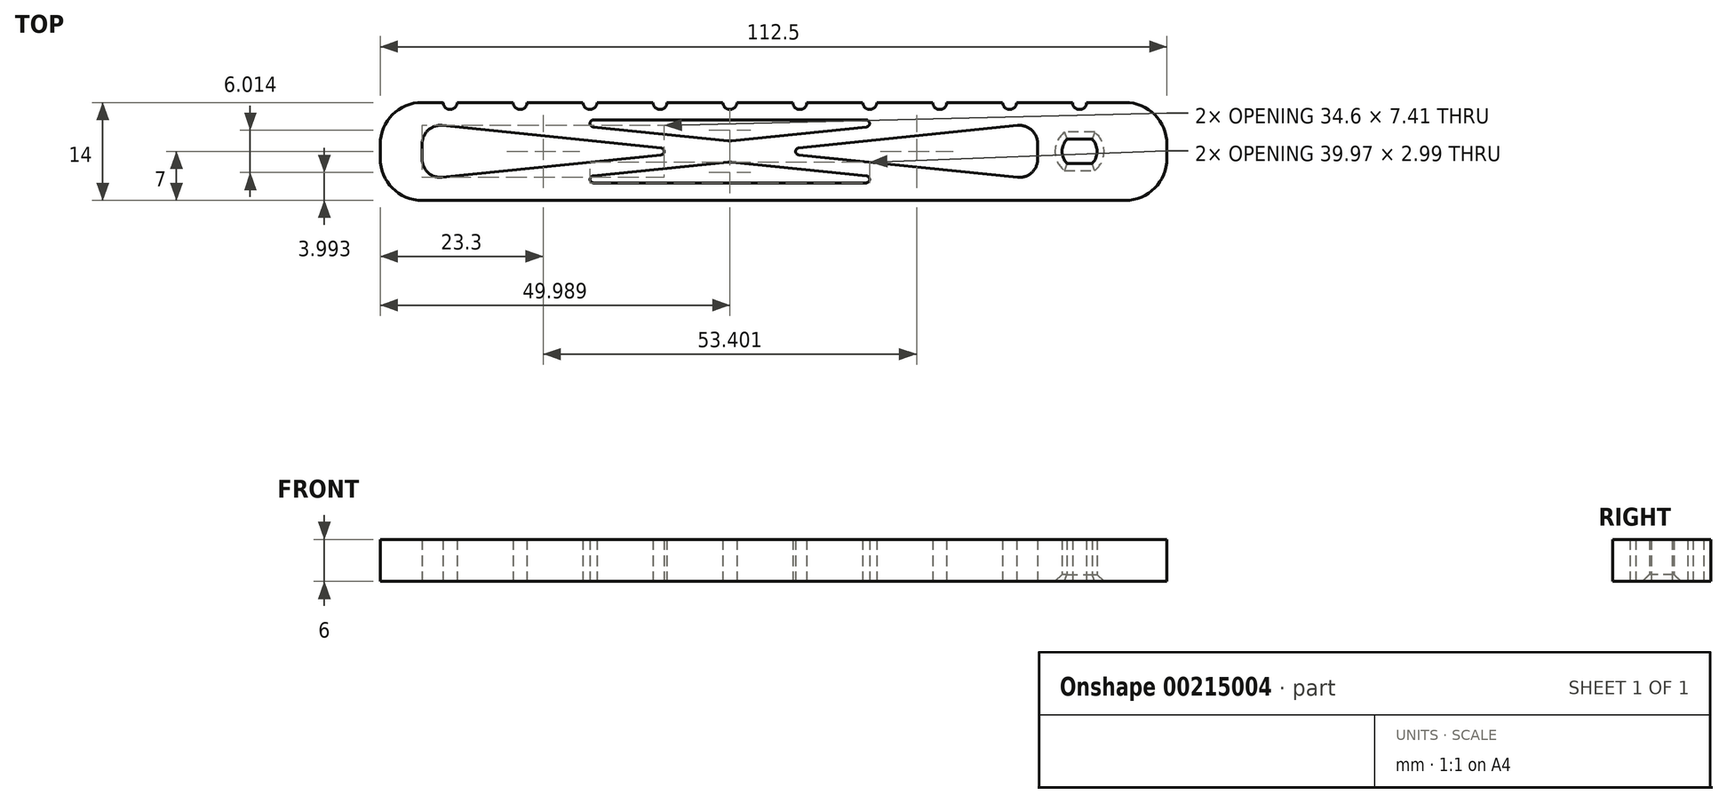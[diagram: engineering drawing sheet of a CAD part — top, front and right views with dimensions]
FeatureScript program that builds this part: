
annotation { "Feature Type Name" : "Feature", "Feature Type Description" : "" }
export const myFeature = defineFeature(function(context is Context, id is Id, definition is map)
    precondition{}
    {
        {
            var Q0;
            Q0=qCreatedBy(makeId("Top.planeOp"),FACE);
            var sketch = newSketch(context, id + "F0", { "sketchPlane" : qUnion([Q0])});
            skLineSegment(sketch, "E0.bottom", {"start": v(-94, 7) * mm, "end": v(-91, 7) * mm});
            skLineSegment(sketch, "E0.top", {"start": v(-94, -7) * mm, "end": v(6.5, -7) * mm});
            skLineSegment(sketch, "E0.left", {"start": v(-100, 1) * mm, "end": v(-100, -1) * mm});
            skLineSegment(sketch, "E0.right", {"start": v(12.5, 1) * mm, "end": v(12.5, -1) * mm});
            skArc(sketch, "E1", {"start": v(-1.79, 1.75) * mm, "mid": v(-2.5, 0) * mm, "end": v(-1.79, -1.75) * mm});
            skLineSegment(sketch, "E2.bottom", {"start": v(-1.79, 1.75) * mm, "end": v(1.79, 1.75) * mm});
            skLineSegment(sketch, "E2.top", {"start": v(-1.79, -1.75) * mm, "end": v(1.79, -1.75) * mm});
            skArc(sketch, "E3.trimOffspring", {"start": v(1.79, -1.75) * mm, "mid": v(2.5, 0) * mm, "end": v(1.79, 1.75) * mm});
            skPoint(sketch, "E4.visualSharp", {"position": v(12.5, 7) * mm});
            skArc(sketch, "E4.filletArc", {"start": v(12.5, 1) * mm, "mid": v(10.74, 5.24) * mm, "end": v(6.5, 7) * mm});
            skPoint(sketch, "E5.visualSharp", {"position": v(12.5, -7) * mm});
            skArc(sketch, "E5.filletArc", {"start": v(6.5, -7) * mm, "mid": v(10.74, -5.24) * mm, "end": v(12.5, -1) * mm});
            skPoint(sketch, "E6.visualSharp", {"position": v(-100, 7) * mm});
            skArc(sketch, "E6.filletArc", {"start": v(-94, 7) * mm, "mid": v(-98.24, 5.24) * mm, "end": v(-100, 1) * mm});
            skPoint(sketch, "E7.visualSharp", {"position": v(-100, -7) * mm});
            skArc(sketch, "E7.filletArc", {"start": v(-100, -1) * mm, "mid": v(-98.24, -5.24) * mm, "end": v(-94, -7) * mm});
            skArc(sketch, "E8", {"start": v(-1, 7) * mm, "mid": v(0, 6) * mm, "end": v(1, 7) * mm});
            skLineSegment(sketch, "E9.trimOffspring", {"start": v(1, 7) * mm, "end": v(6.5, 7) * mm});
            skArc(sketch, "E10.1.0.0", {"start": v(-11, 7) * mm, "mid": v(-10, 6) * mm, "end": v(-9, 7) * mm});
            skArc(sketch, "E10.2.0.0", {"start": v(-21, 7) * mm, "mid": v(-20, 6) * mm, "end": v(-19, 7) * mm});
            skArc(sketch, "E10.3.0.0", {"start": v(-31, 7) * mm, "mid": v(-30, 6) * mm, "end": v(-29, 7) * mm});
            skArc(sketch, "E10.4.0.0", {"start": v(-41, 7) * mm, "mid": v(-40, 6) * mm, "end": v(-39, 7) * mm});
            skArc(sketch, "E10.5.0.0", {"start": v(-51, 7) * mm, "mid": v(-50, 6) * mm, "end": v(-49, 7) * mm});
            skArc(sketch, "E10.6.0.0", {"start": v(-61, 7) * mm, "mid": v(-60, 6) * mm, "end": v(-59, 7) * mm});
            skArc(sketch, "E10.7.0.0", {"start": v(-71, 7) * mm, "mid": v(-70, 6) * mm, "end": v(-69, 7) * mm});
            skArc(sketch, "E10.8.0.0", {"start": v(-81, 7) * mm, "mid": v(-80, 6) * mm, "end": v(-79, 7) * mm});
            skArc(sketch, "E10.9.0.0", {"start": v(-91, 7) * mm, "mid": v(-90, 6) * mm, "end": v(-89, 7) * mm});
            skLineSegment(sketch, "E11.trimOffspring", {"start": v(-89, 7) * mm, "end": v(-81, 7) * mm});
            skLineSegment(sketch, "E12.trimOffspring", {"start": v(-79, 7) * mm, "end": v(-71, 7) * mm});
            skLineSegment(sketch, "E13.trimOffspring", {"start": v(-69, 7) * mm, "end": v(-61, 7) * mm});
            skLineSegment(sketch, "E14.trimOffspring", {"start": v(-59, 7) * mm, "end": v(-51, 7) * mm});
            skLineSegment(sketch, "E15.trimOffspring", {"start": v(-49, 7) * mm, "end": v(-41, 7) * mm});
            skLineSegment(sketch, "E16.trimOffspring", {"start": v(-39, 7) * mm, "end": v(-31, 7) * mm});
            skLineSegment(sketch, "E17.trimOffspring", {"start": v(-29, 7) * mm, "end": v(-21, 7) * mm});
            skLineSegment(sketch, "E18.trimOffspring", {"start": v(-19, 7) * mm, "end": v(-11, 7) * mm});
            skLineSegment(sketch, "E19.trimOffspring", {"start": v(-9, 7) * mm, "end": v(-1, 7) * mm});
            skLineSegment(sketch, "E20", {"start": v(-94, 1.12) * mm, "end": v(-94, -1.12) * mm});
            skLineSegment(sketch, "E21", {"start": v(-91.13, -3.7) * mm, "end": v(-59.85, -0.5) * mm});
            skLineSegment(sketch, "E22", {"start": v(-59.85, 0.5) * mm, "end": v(-91.13, 3.7) * mm});
            skLineSegment(sketch, "E23", {"start": v(-40.15, 0.5) * mm, "end": v(-8.87, 3.7) * mm});
            skLineSegment(sketch, "E24", {"start": v(-6, 1.12) * mm, "end": v(-6, -1.12) * mm});
            skLineSegment(sketch, "E25", {"start": v(-8.87, -3.7) * mm, "end": v(-40.15, -0.5) * mm});
            skLineSegment(sketch, "E26", {"start": v(-69.5, 4.5) * mm, "end": v(-30.53, 4.5) * mm});
            skLineSegment(sketch, "E27", {"start": v(-30.47, 3.5) * mm, "end": v(-49.76, 1.53) * mm});
            skLineSegment(sketch, "E28", {"start": v(-50.29, 1.53) * mm, "end": v(-69.55, 3.5) * mm});
            skLineSegment(sketch, "E29", {"start": v(-69.55, -3.5) * mm, "end": v(-50.29, -1.53) * mm});
            skLineSegment(sketch, "E30", {"start": v(-49.76, -1.53) * mm, "end": v(-30.47, -3.5) * mm});
            skLineSegment(sketch, "E31", {"start": v(-30.53, -4.5) * mm, "end": v(-69.5, -4.5) * mm});
            skPoint(sketch, "E32.visualSharp", {"position": v(-94, 4) * mm});
            skArc(sketch, "E32.filletArc", {"start": v(-91.13, 3.7) * mm, "mid": v(-93.14, 3.05) * mm, "end": v(-94, 1.12) * mm});
            skPoint(sketch, "E33.visualSharp", {"position": v(-94, -4) * mm});
            skArc(sketch, "E33.filletArc", {"start": v(-94, -1.12) * mm, "mid": v(-93.14, -3.05) * mm, "end": v(-91.13, -3.7) * mm});
            skPoint(sketch, "E34.visualSharp", {"position": v(-50.02, -1.5) * mm});
            skArc(sketch, "E34.filletArc", {"start": v(-49.76, -1.53) * mm, "mid": v(-50.02, -1.51) * mm, "end": v(-50.29, -1.53) * mm});
            skPoint(sketch, "E35.visualSharp", {"position": v(-50.02, 1.5) * mm});
            skArc(sketch, "E35.filletArc", {"start": v(-50.29, 1.53) * mm, "mid": v(-50.02, 1.51) * mm, "end": v(-49.76, 1.53) * mm});
            skPoint(sketch, "E36.visualSharp", {"position": v(-6, 4) * mm});
            skArc(sketch, "E36.filletArc", {"start": v(-6, 1.12) * mm, "mid": v(-6.86, 3.05) * mm, "end": v(-8.87, 3.7) * mm});
            skPoint(sketch, "E37.visualSharp", {"position": v(-6, -4) * mm});
            skArc(sketch, "E37.filletArc", {"start": v(-8.87, -3.7) * mm, "mid": v(-6.86, -3.05) * mm, "end": v(-6, -1.12) * mm});
            skPoint(sketch, "E38.visualSharp", {"position": v(-55, 0) * mm});
            skArc(sketch, "E38.filletArc", {"start": v(-59.85, -0.5) * mm, "mid": v(-59.4, 0) * mm, "end": v(-59.85, 0.5) * mm});
            skPoint(sketch, "E39.visualSharp", {"position": v(-79.27, 4.5) * mm});
            skArc(sketch, "E39.filletArc", {"start": v(-69.5, 4.5) * mm, "mid": v(-70, 4.03) * mm, "end": v(-69.55, 3.5) * mm});
            skPoint(sketch, "E40.visualSharp", {"position": v(-79.27, -4.5) * mm});
            skArc(sketch, "E40.filletArc", {"start": v(-69.55, -3.5) * mm, "mid": v(-70, -4.03) * mm, "end": v(-69.5, -4.5) * mm});
            skPoint(sketch, "E41.visualSharp", {"position": v(-20.74, 4.5) * mm});
            skArc(sketch, "E41.filletArc", {"start": v(-30.47, 3.5) * mm, "mid": v(-30.03, 4.03) * mm, "end": v(-30.53, 4.5) * mm});
            skPoint(sketch, "E42.visualSharp", {"position": v(-20.74, -4.5) * mm});
            skArc(sketch, "E42.filletArc", {"start": v(-30.53, -4.5) * mm, "mid": v(-30.03, -4.03) * mm, "end": v(-30.47, -3.5) * mm});
            skPoint(sketch, "E43.visualSharp", {"position": v(-45, 0) * mm});
            skArc(sketch, "E43.filletArc", {"start": v(-40.15, 0.5) * mm, "mid": v(-40.6, 0) * mm, "end": v(-40.15, -0.5) * mm});
            skSolve(sketch);
        }
        {
            var Q0;
            Q0 = qSketchRegion(id + "F0", true);
            extrude(context, id + "F1", {"entities" : qUnion([Q0]), "depth" : 6 * mm});
        }
        {
            var Q0;
            Q0=makeQuery(id+"F1.opExtrude","CAP_EDGE",EDGE,{"disambiguationData":[OSD([sQuery(id+"F0.wireOp",EDGE,"E2.bottom")])],"isStart":true});
            var Q1;
            Q1=makeQuery(id+"F1.opExtrude","CAP_EDGE",EDGE,{"disambiguationData":[OSD([sQuery(id+"F0.wireOp",EDGE,"E1")])],"isStart":true});
            var Q2;
            Q2=makeQuery(id+"F1.opExtrude","CAP_EDGE",EDGE,{"disambiguationData":[OSD([sQuery(id+"F0.wireOp",EDGE,"E3.trimOffspring")])],"isStart":true});
            var Q3;
            Q3=makeQuery(id+"F1.opExtrude","CAP_EDGE",EDGE,{"disambiguationData":[OSD([sQuery(id+"F0.wireOp",EDGE,"E2.top")])],"isStart":true});
            chamfer(context, id + "F2", {"entities" : qUnion([Q0, Q1, Q2, Q3]), "width" : 1 * mm, "tangentPropagation" : true});
        }
    });
